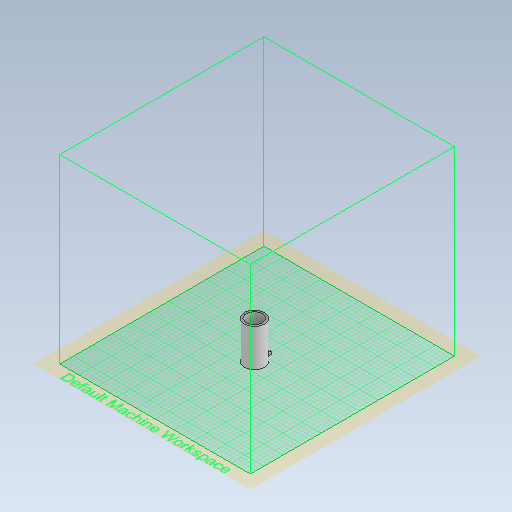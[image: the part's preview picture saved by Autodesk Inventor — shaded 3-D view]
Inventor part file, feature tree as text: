
AUTODESK INVENTOR PART (.ipt)
format: ipt  version: 2021 (Build 250183000, 183)  size: 580,096 bytes
history: native  units: in
note: dims shown in document units (in); Inventor stores cm internally (conversion verified against a paired STEP export)
features: projected_geometry x11, extrude x9, sketch x5, chamfer x3, fillet x2, plane x1, pattern_linear x1
ambient origin geometry x8: Origin, YZ Plane, XZ Plane, XY Plane, X Axis, Y Axis, Z Axis, Center Point
bodies: Solid1 (feature_tree)
feature tree (32):
  extrude  "Extrusion1"  Depth=3.2677in TaperAngle=0.0deg
  plane  "Work Plane1"
  extrude  "Extrusion7"  Depth=3.189in TaperAngle=0.0deg
  extrude  "Extrusion8"  Depth=0.3937in
  extrude  "Extrusion9"  Depth=0.3937in
  extrude  "Extrusion10"  Depth=0.3937in TaperAngle=0.0deg
  extrude  "Extrusion11"  Depth=0.3937in
  extrude  "Extrusion12"  Depth=0.3937in
  pattern_linear  "Rectangular Pattern3"  Spacing1=0.1969in  [1 undecoded]
  extrude  "Extrusion13"  Depth=0.3937in TaperAngle=0.0deg
  chamfer  "Chamfer2"  Distance=1.811in
  chamfer  "Chamfer4"  Distance=0.0394in
  chamfer  "Chamfer5"  Distance=0.0098in
  extrude  "Extrusion14"  Depth=0.0787in
  fillet  "Fillet11"  Radius=0.1181in
  fillet  "Fillet12"  Radius=0.3937in
  sketch  "Sketch2"  dims[d2=1.752in d3=3.2677in d4=0.0in]
  sketch  "Sketch9"  dims[d54=1.4173in d55=3.189in d56=0.0in]
  projected_geometry  "Projected Loop7"
  sketch  "Sketch10"  dims[d57=0.3937in d58=0.2756in]
  projected_geometry  "Projected Loop8"
  projected_geometry  "Projected Loop9"
  projected_geometry  "Projected Loop10"
  projected_geometry  "Projected Loop11"
  projected_geometry  "Projected Loop12"
  projected_geometry  "Projected Loop14"
  projected_geometry  "Projected Loop15"
  sketch  "Sketch16"  dims[d59=0.3937in d60=0.0236in d61=0.0in d62=0.0in d63=0.2047in]
  projected_geometry  "Projected Loop16"
  sketch  "Sketch17"  dims[d64=0.126in d66=0.0295in d67=0.0in d68=0.0591in d69=0.0591in d71=0.1969in d72=0.0in d76=1.1811in d77=0.0in d84=1.811in d85=0.0394in d86=0.0098in d87=0.0in d88=8.2677in d90=0.0787in d92=0.1181in d93=0.3937in d94=0.0in d96=0.0059in d97=0.0185in d98=0.0787in d99=45.0deg d103=0.1575in d104=0.0787in d105=45.0deg d106=0.0098in d107=0.0787in d108=45.0deg d109=0.2756in d110=0.0315in d111=0.0in d116=0.4724in d117=0.3937in d19=0.0197in d20=0.0344in d21=0.0197in d22=0.0344in]
  projected_geometry  "Projected Loop17"
  projected_geometry  "Projected Loop18"
note: 1 required parameter value undecoded (feature->parameter linkage not recoverable at this tier; creation-order binding heuristic only, values carry confidence <= 0.55)
